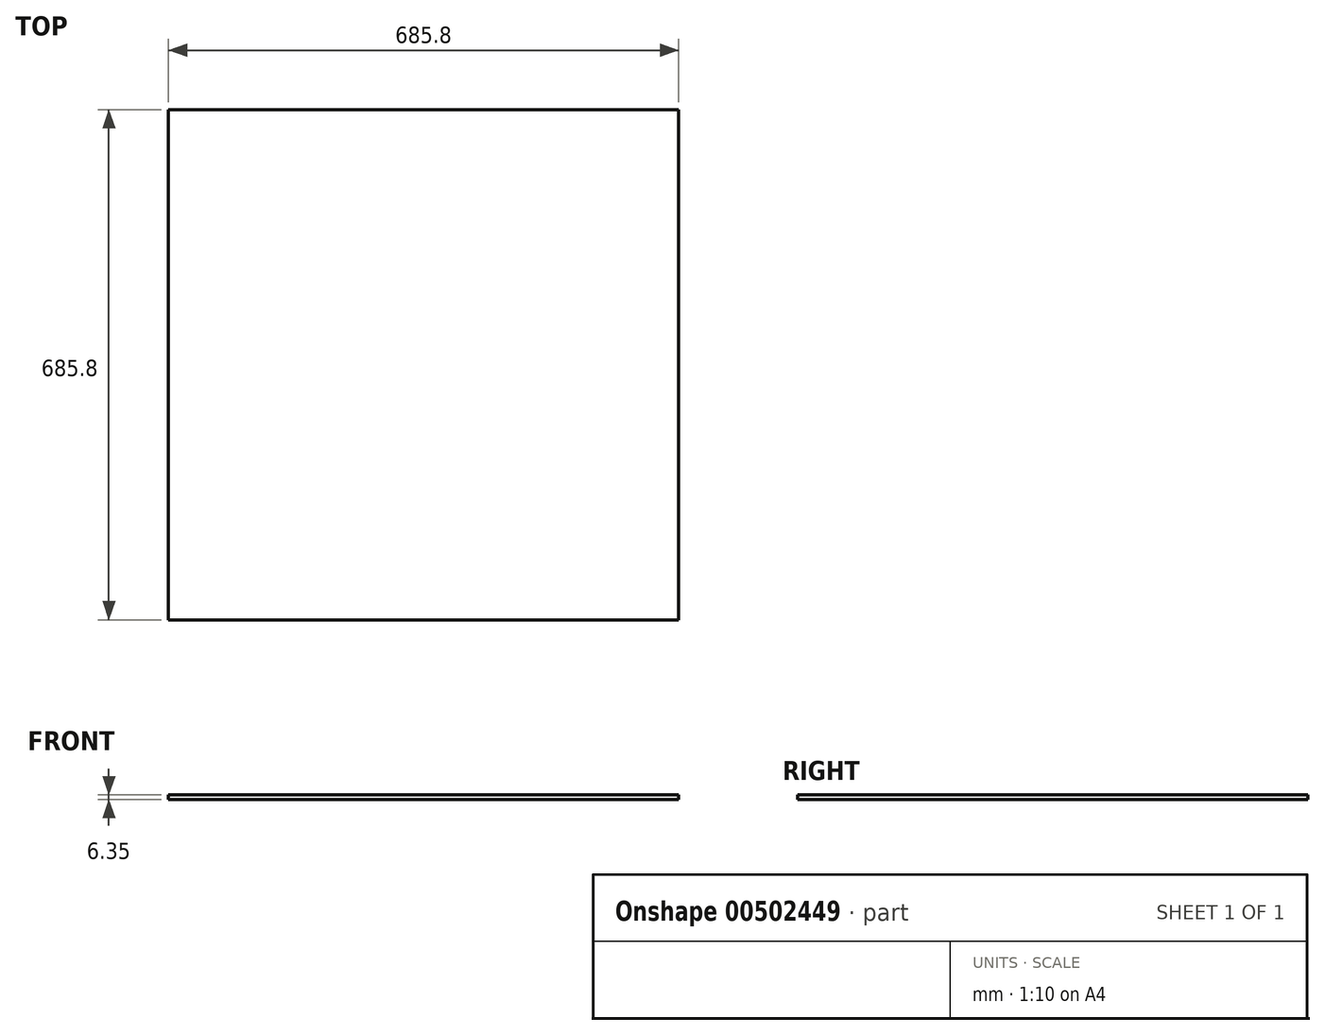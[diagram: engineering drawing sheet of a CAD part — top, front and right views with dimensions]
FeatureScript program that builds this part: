
annotation { "Feature Type Name" : "Feature", "Feature Type Description" : "" }
export const myFeature = defineFeature(function(context is Context, id is Id, definition is map)
    precondition{}
    {
        {
            var Q0;
            Q0=qCreatedBy(makeId("Top.planeOp"),FACE);
            var sketch = newSketch(context, id + "F0", { "sketchPlane" : qUnion([Q0])});
            skLineSegment(sketch, "E0.bottom", {"start": v(0, 685.8) * mm, "end": v(685.8, 685.8) * mm});
            skLineSegment(sketch, "E0.top", {"start": v(0, 0) * mm, "end": v(685.8, 0) * mm});
            skLineSegment(sketch, "E0.left", {"start": v(0, 685.8) * mm, "end": v(0, 0) * mm});
            skLineSegment(sketch, "E0.right", {"start": v(685.8, 685.8) * mm, "end": v(685.8, 0) * mm});
            skSolve(sketch);
        }
        {
            var Q0;
            Q0=makeQuery(id+"F0.imprint","IMPRINT",FACE,{"disambiguationData":[TD([[makeQuery(id+"F0.imprint","IMPRINT",EDGE,{"derivedFrom":sQuery(id+"F0.wireOp",EDGE,"E0.bottom")}),-1.0]])]});
            extrude(context, id + "F1", {"entities" : qUnion([Q0]), "depth" : 6.35 * mm});
        }
    });
